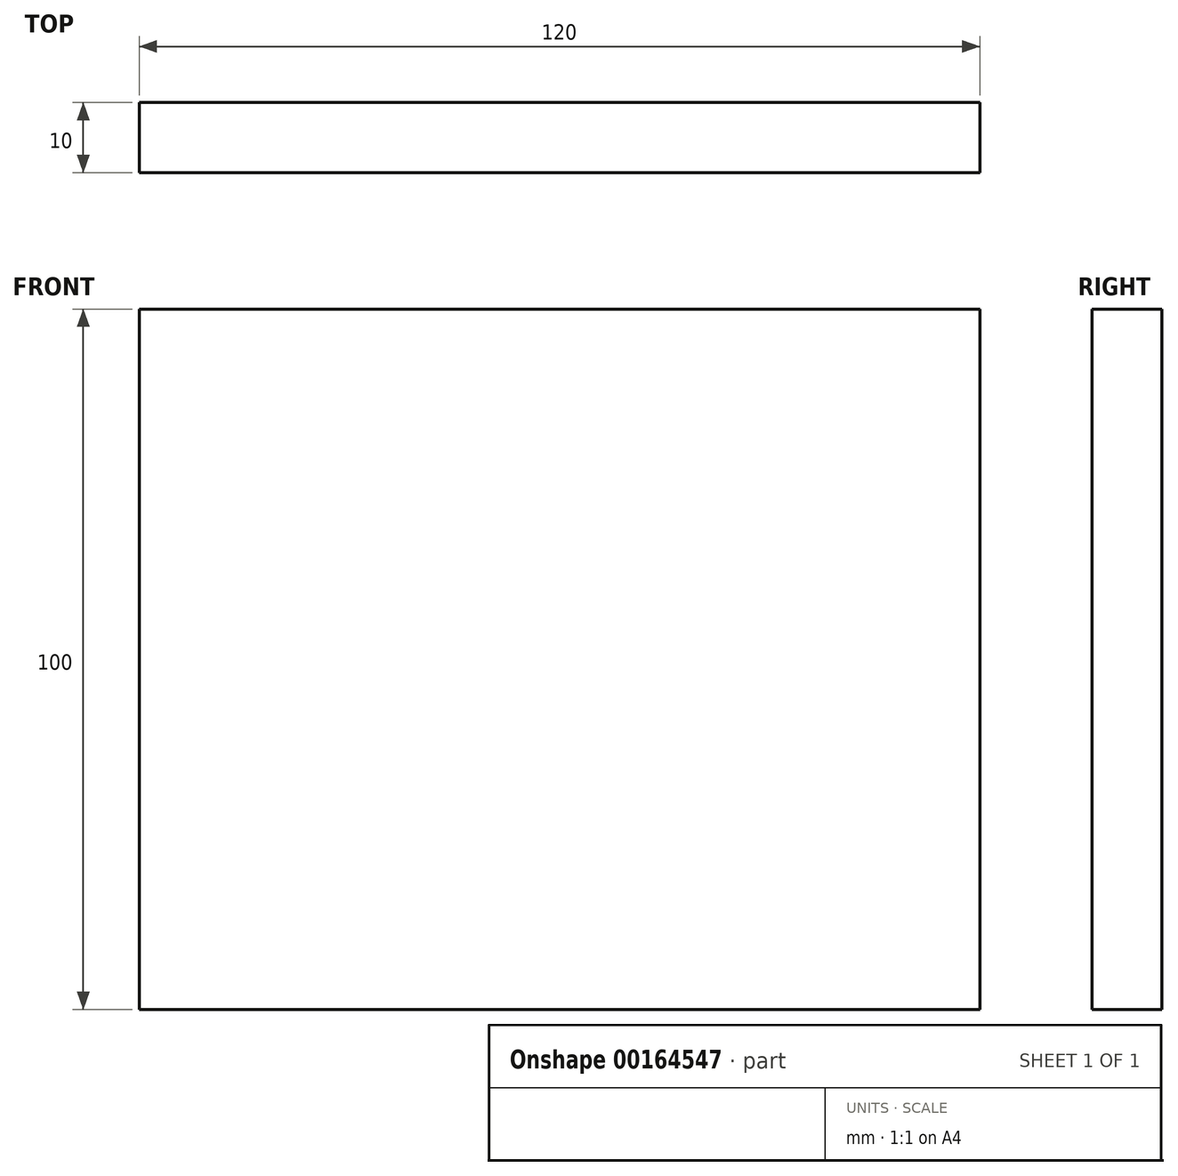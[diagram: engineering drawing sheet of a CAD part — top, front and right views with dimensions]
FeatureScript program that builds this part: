
annotation { "Feature Type Name" : "Feature", "Feature Type Description" : "" }
export const myFeature = defineFeature(function(context is Context, id is Id, definition is map)
    precondition{}
    {
        {
            var Q0;
            Q0=qCreatedBy(makeId("Top.planeOp"),FACE);
            var sketch = newSketch(context, id + "F0", { "sketchPlane" : qUnion([Q0])});
            skArc(sketch, "E0", {"start": v(60, 0) * mm, "mid": v(0, 60) * mm, "end": v(-60, 0) * mm});
            skLineSegment(sketch, "E1", {"start": v(-60, 0) * mm, "end": v(60, 0) * mm});
            skLineSegment(sketch, "E2", {"start": v(-60, 0) * mm, "end": v(-60, -10) * mm});
            skLineSegment(sketch, "E3", {"start": v(60, 0) * mm, "end": v(60, -10) * mm});
            skLineSegment(sketch, "E4", {"start": v(-60, -10) * mm, "end": v(60, -10) * mm});
            skSolve(sketch);
        }
        {
            var Q0;
            Q0=makeQuery(id+"F0.imprint","IMPRINT",FACE,{"disambiguationData":[TD([[makeQuery(id+"F0.imprint","IMPRINT",EDGE,{"derivedFrom":sQuery(id+"F0.wireOp",EDGE,"E1")}),-1.0]])]});
            extrude(context, id + "F1", {"entities" : qUnion([Q0]), "depth" : 100 * mm});
        }
    });
